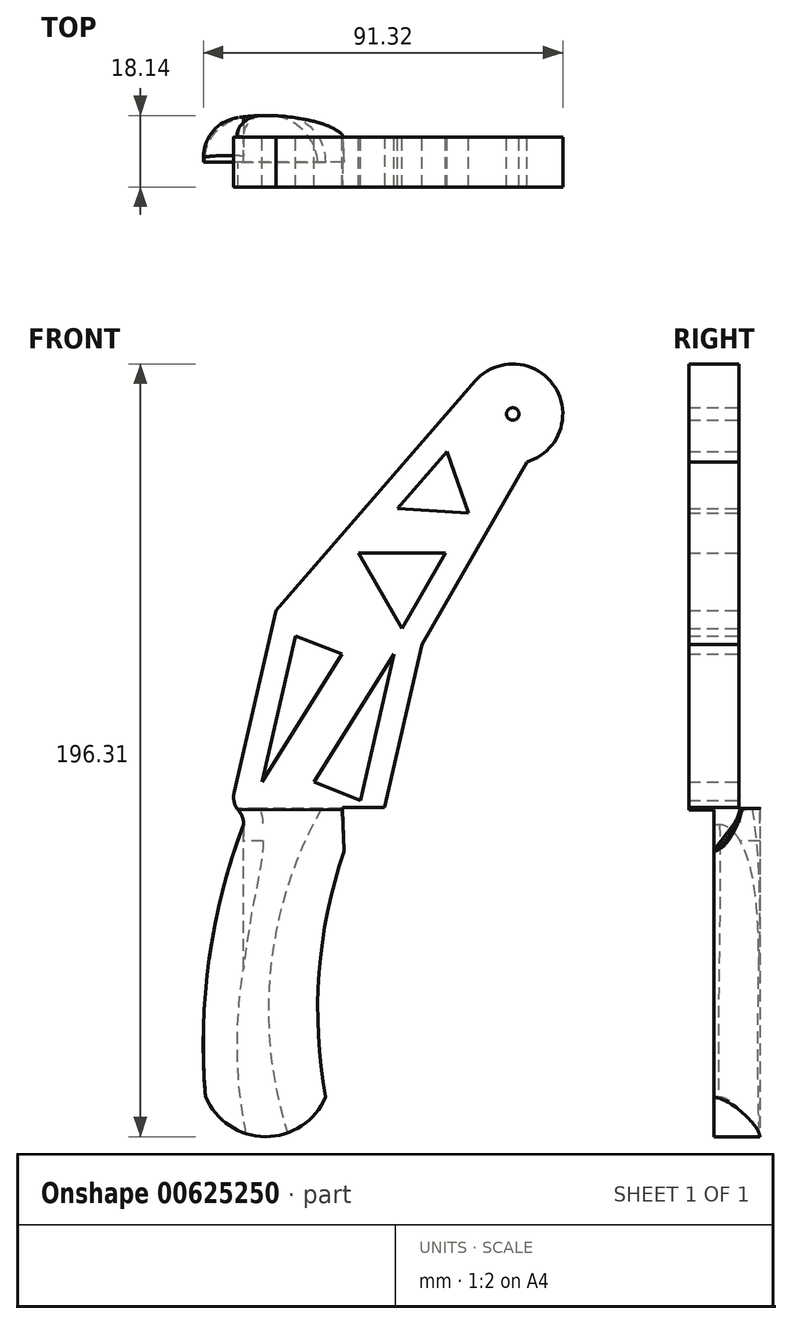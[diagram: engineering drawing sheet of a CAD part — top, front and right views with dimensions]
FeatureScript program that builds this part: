
annotation { "Feature Type Name" : "Feature", "Feature Type Description" : "" }
export const myFeature = defineFeature(function(context is Context, id is Id, definition is map)
    precondition{}
    {
        {
            var Q0;
            Q0=qCreatedBy(makeId("Front.planeOp"),FACE);
            var sketch = newSketch(context, id + "F0", { "sketchPlane" : qUnion([Q0])});
            skArc(sketch, "E0", {"start": v(128.28, -19.7) * mm, "mid": v(135.4, -0.67) * mm, "end": v(115.12, 0.81) * mm});
            skCircle(sketch, "E1", {"center": v(124.7, -7.52) * mm, "radius": 1.59 * mm});
            skLineSegment(sketch, "E2", {"start": v(115.12, 0.81) * mm, "end": v(64.49, -57.4) * mm});
            skLineSegment(sketch, "E3", {"start": v(64.49, -57.4) * mm, "end": v(53.2, -106.93) * mm});
            skLineSegment(sketch, "E4", {"start": v(128.28, -19.7) * mm, "end": v(101.6, -66.02) * mm});
            skPoint(sketch, "E4.endSnap0", {"position": v(101.6, 0) * mm});
            skLineSegment(sketch, "E5", {"start": v(101.6, -66.02) * mm, "end": v(92, -108.12) * mm});
            skArc(sketch, "E6", {"start": v(56.3, -111.86) * mm, "mid": v(47.6, -145.85) * mm, "end": v(46.64, -180.91) * mm});
            skLineSegment(sketch, "E7", {"start": v(53.2, -106.93) * mm, "end": v(56.3, -107.64) * mm});
            skLineSegment(sketch, "E8", {"start": v(56.3, -107.64) * mm, "end": v(56.3, -111.86) * mm});
            skLineSegment(sketch, "E9", {"start": v(92, -108.12) * mm, "end": v(85.97, -108.03) * mm});
            skArc(sketch, "E10", {"start": v(85.97, -108.03) * mm, "mid": v(76.06, -143.88) * mm, "end": v(77.12, -181.07) * mm});
            skArc(sketch, "E11", {"start": v(46.64, -180.91) * mm, "mid": v(61.83, -191.13) * mm, "end": v(77.12, -181.07) * mm});
            skLineSegment(sketch, "E12", {"start": v(107.95, -17.1) * mm, "end": v(95.44, -31.48) * mm});
            skLineSegment(sketch, "E13", {"start": v(107.95, -17.1) * mm, "end": v(113.5, -32.63) * mm});
            skLineSegment(sketch, "E14", {"start": v(95.44, -31.48) * mm, "end": v(113.5, -32.63) * mm});
            skLineSegment(sketch, "E15", {"start": v(107.61, -42.86) * mm, "end": v(96.59, -62) * mm});
            skPoint(sketch, "E15.startSnap0", {"position": v(114.94, -42.86) * mm});
            skLineSegment(sketch, "E16", {"start": v(96.59, -62) * mm, "end": v(85.53, -42.89) * mm});
            skLineSegment(sketch, "E17", {"start": v(85.53, -42.89) * mm, "end": v(107.61, -42.86) * mm});
            skLineSegment(sketch, "E18", {"start": v(69.52, -63.9) * mm, "end": v(61.05, -101.04) * mm});
            skLineSegment(sketch, "E19", {"start": v(61.05, -101.04) * mm, "end": v(81.35, -68.5) * mm});
            skLineSegment(sketch, "E20", {"start": v(81.35, -68.5) * mm, "end": v(69.52, -63.9) * mm});
            skLineSegment(sketch, "E21", {"start": v(94.52, -68.5) * mm, "end": v(74.22, -101.04) * mm});
            skLineSegment(sketch, "E22", {"start": v(74.22, -101.04) * mm, "end": v(86.05, -105.65) * mm});
            skLineSegment(sketch, "E23", {"start": v(86.05, -105.65) * mm, "end": v(94.52, -68.5) * mm});
            skSolve(sketch);
        }
        {
            var Q0;
            Q0 = qSketchRegion(id + "F0", true);
            extrude(context, id + "F1", {"entities" : qUnion([Q0]), "depth" : 19.05 * mm, "offsetDistance" : 25.4 * mm});
        }
        {
            var Q0;
            Q0=makeQuery(id+"F1.opExtrude","SWEPT_EDGE",EDGE,{"disambiguationData":[OSD([sQuery(id+"F0.wireOp",EDGE,"E7"),sQuery(id+"F0.wireOp",EDGE,"E8")])]});
            fillet(context, id + "F2", {"entities" : qUnion([Q0]), "radius" : 5.08 * mm, "tangentPropagation" : true, "allowEdgeOverflow" : false});
        }
        {
            var Q0;
            Q0=makeQuery(id+"F2.opFillet","BLEND_EDGE",EDGE,{"blendedFrom":[makeQuery(id+"F1.opExtrude","SWEPT_EDGE",EDGE,{"disambiguationData":[OSD([sQuery(id+"F0.wireOp",EDGE,"E7"),sQuery(id+"F0.wireOp",EDGE,"E8")])]}),makeQuery(id+"F1.opExtrude","SWEPT_FACE",FACE,{"disambiguationData":[OSD([sQuery(id+"F0.wireOp",EDGE,"E3")])]})],"blendedInto":[makeQuery(id+"F1.opExtrude","SWEPT_FACE",FACE,{"disambiguationData":[OSD([sQuery(id+"F0.wireOp",EDGE,"E3")])]})]});
            fillet(context, id + "F3", {"entities" : qUnion([Q0]), "radius" : 5.08 * mm, "tangentPropagation" : true, "allowEdgeOverflow" : false});
        }
        {
            var Q0;
            Q0=qCreatedBy(makeId("Top.planeOp"),FACE);
            cPlane(context, id + "F4", {"entities" : qUnion([Q0]), "cplaneType" : CPlaneType.OFFSET, "offset" : 192.53 * mm, "oppositeDirection" : true, "width" : 152.4 * mm, "height" : 152.4 * mm});
        }
        {
            var Q0;
            Q0=qCreatedBy(id+"F4.planeOp",FACE);
            var sketch = newSketch(context, id + "F5", { "sketchPlane" : qUnion([Q0])});
            skArc(sketch, "E24", {"start": v(81.46, -11.2) * mm, "mid": v(61.05, -7.27) * mm, "end": v(40.82, -12.06) * mm});
            skLineSegment(sketch, "E25", {"start": v(81.46, -11.2) * mm, "end": v(80.29, 11.88) * mm});
            skLineSegment(sketch, "E26", {"start": v(80.29, 11.88) * mm, "end": v(41.72, 10.68) * mm});
            skLineSegment(sketch, "E27", {"start": v(41.72, 10.68) * mm, "end": v(40.82, -12.06) * mm});
            skSolve(sketch);
        }
        {
            var Q0;
            Q0 = qSketchRegion(id + "F5", true);
            extrude(context, id + "F6", {"entities" : qUnion([Q0]), "operationType" : NewBodyOperationType.REMOVE, "depth" : 84.81 * mm, "offsetDistance" : 25.4 * mm});
        }
        {
            var Q0;
            Q0=makeQuery(id+"F1.opExtrude","CAP_FACE",FACE,{"disambiguationData":[OSD([sQuery(id+"F0.wireOp",EDGE,"E0"),sQuery(id+"F0.wireOp",EDGE,"E1"),sQuery(id+"F0.wireOp",EDGE,"E2"),sQuery(id+"F0.wireOp",EDGE,"E3"),sQuery(id+"F0.wireOp",EDGE,"E4"),sQuery(id+"F0.wireOp",EDGE,"E5"),sQuery(id+"F0.wireOp",EDGE,"E6"),sQuery(id+"F0.wireOp",EDGE,"E7"),sQuery(id+"F0.wireOp",EDGE,"E8"),sQuery(id+"F0.wireOp",EDGE,"E9"),sQuery(id+"F0.wireOp",EDGE,"E10"),sQuery(id+"F0.wireOp",EDGE,"E11"),sQuery(id+"F0.wireOp",EDGE,"E12"),sQuery(id+"F0.wireOp",EDGE,"E13"),sQuery(id+"F0.wireOp",EDGE,"E14"),sQuery(id+"F0.wireOp",EDGE,"E15"),sQuery(id+"F0.wireOp",EDGE,"E16"),sQuery(id+"F0.wireOp",EDGE,"E17"),sQuery(id+"F0.wireOp",EDGE,"E18"),sQuery(id+"F0.wireOp",EDGE,"E19"),sQuery(id+"F0.wireOp",EDGE,"E20"),sQuery(id+"F0.wireOp",EDGE,"E21"),sQuery(id+"F0.wireOp",EDGE,"E22"),sQuery(id+"F0.wireOp",EDGE,"E23")])],"isStart":true});
            var sketch = newSketch(context, id + "F7", { "sketchPlane" : qUnion([Q0])});
            skLineSegment(sketch, "E28", {"start": v(-80.9, -107.72) * mm, "end": v(-85.97, -108.03) * mm});
            skLineSegment(sketch, "E29", {"start": v(-85.97, -108.03) * mm, "end": v(-88.9, -122.3) * mm});
            skLineSegment(sketch, "E30", {"start": v(-88.9, -122.3) * mm, "end": v(-80.76, -122.3) * mm});
            skLineSegment(sketch, "E31", {"start": v(-80.76, -122.3) * mm, "end": v(-80.9, -107.72) * mm});
            skSolve(sketch);
        }
        {
            var Q0;
            Q0 = qSketchRegion(id + "F7", true);
            extrude(context, id + "F8", {"entities" : qUnion([Q0]), "operationType" : NewBodyOperationType.REMOVE, "oppositeDirection" : true, "depth" : 10.92 * mm, "offsetDistance" : 25.4 * mm});
        }
        {
            var Q0;
            Q0=makeQuery(id+"F6.boolean.opBoolean","COPY",FACE,{"derivedFrom":makeQuery(id+"F6.opExtrude","SWEPT_FACE",FACE,{"disambiguationData":[OSD([sQuery(id+"F5.wireOp",EDGE,"E25")])]})});
            var sketch = newSketch(context, id + "F9", { "sketchPlane" : qUnion([Q0])});
            skArc(sketch, "E32", {"start": v(16.7, -109.3) * mm, "mid": v(19.05, -114.53) * mm, "end": v(23.2, -118.49) * mm});
            skLineSegment(sketch, "E33", {"start": v(16.7, -109.3) * mm, "end": v(8.62, -109.3) * mm});
            skLineSegment(sketch, "E34", {"start": v(8.62, -109.3) * mm, "end": v(7.9, -127.1) * mm});
            skLineSegment(sketch, "E35", {"start": v(7.9, -127.1) * mm, "end": v(23.2, -118.49) * mm});
            skSolve(sketch);
        }
        {
            var Q0;
            Q0 = qSketchRegion(id + "F9", true);
            extrude(context, id + "F10", {"entities" : qUnion([Q0]), "operationType" : NewBodyOperationType.REMOVE, "oppositeDirection" : true, "depth" : 25.4 * mm, "offsetDistance" : 25.4 * mm});
        }
        {
            var Q0;
            Q0=makeQuery(id+"F10.boolean.opBoolean","INTERSECT",EDGE,{"derivedFrom":[makeQuery(id+"F1.opExtrude","SWEPT_FACE",FACE,{"disambiguationData":[OSD([sQuery(id+"F0.wireOp",EDGE,"E10")])]}),makeQuery(id+"F10.opExtrude","SWEPT_FACE",FACE,{"disambiguationData":[OSD([sQuery(id+"F9.wireOp",EDGE,"E32")])]})]});
            fillet(context, id + "F11", {"entities" : qUnion([Q0]), "radius" : 7.62 * mm, "tangentPropagation" : true, "allowEdgeOverflow" : false});
        }
        {
            var Q0;
            Q0=makeQuery(id+"F10.boolean.opBoolean","INTERSECT",EDGE,{"derivedFrom":[makeQuery(id+"F1.opExtrude","SWEPT_FACE",FACE,{"disambiguationData":[OSD([sQuery(id+"F0.wireOp",EDGE,"E10")])]}),makeQuery(id+"F10.opExtrude","SWEPT_FACE",FACE,{"disambiguationData":[OSD([sQuery(id+"F9.wireOp",EDGE,"E33")])]})]});
            fillet(context, id + "F12", {"entities" : qUnion([Q0]), "radius" : 5.08 * mm, "tangentPropagation" : true, "allowEdgeOverflow" : false});
        }
        {
            var Q0;
            {var subQ1=sQuery(id+"F7.wireOp",EDGE,"E28");var subQ2=makeQuery(id+"F1.opExtrude","SWEPT_FACE",FACE,{"disambiguationData":[OSD([sQuery(id+"F0.wireOp",EDGE,"E10")])]});Q0=makeQuery(id+"F12.opFillet","BLEND_EDGE",EDGE,{"blendedFrom":[makeQuery(id+"F10.boolean.opBoolean","INTERSECT",EDGE,{"derivedFrom":[subQ2,makeQuery(id+"F10.opExtrude","SWEPT_FACE",FACE,{"disambiguationData":[OSD([sQuery(id+"F9.wireOp",EDGE,"E33")])]})]}),makeQuery(id+"F8.boolean.opBoolean","COPY",FACE,{"disambiguationData":[TD([makeQuery(id+"F1.opExtrude","SWEPT_FACE",FACE,{"disambiguationData":[OSD([sQuery(id+"F0.wireOp",EDGE,"E9")])]})])],"derivedFrom":makeQuery(id+"F8.opExtrude","CAP_FACE",FACE,{"disambiguationData":[OSD([subQ1,sQuery(id+"F7.wireOp",EDGE,"E29"),sQuery(id+"F7.wireOp",EDGE,"E30"),sQuery(id+"F7.wireOp",EDGE,"E31")])],"isStart":false})})],"blendedInto":[makeQuery(id+"F8.boolean.opBoolean","COPY",FACE,{"disambiguationData":[TD([makeQuery(id+"F1.opExtrude","SWEPT_FACE",FACE,{"disambiguationData":[OSD([sQuery(id+"F0.wireOp",EDGE,"E9")])]})])],"derivedFrom":makeQuery(id+"F8.opExtrude","CAP_FACE",FACE,{"disambiguationData":[OSD([subQ1,sQuery(id+"F7.wireOp",EDGE,"E29"),sQuery(id+"F7.wireOp",EDGE,"E30"),sQuery(id+"F7.wireOp",EDGE,"E31")])],"isStart":false})})]});}
            var Q1;
            {var subQ1=sQuery(id+"F7.wireOp",EDGE,"E28");Q1=makeQuery(id+"F10.boolean.opBoolean","INTERSECT",EDGE,{"derivedFrom":[makeQuery(id+"F8.boolean.opBoolean","COPY",FACE,{"disambiguationData":[TD([makeQuery(id+"F1.opExtrude","SWEPT_FACE",FACE,{"disambiguationData":[OSD([sQuery(id+"F0.wireOp",EDGE,"E9")])]})])],"derivedFrom":makeQuery(id+"F8.opExtrude","CAP_FACE",FACE,{"disambiguationData":[OSD([subQ1,sQuery(id+"F7.wireOp",EDGE,"E29"),sQuery(id+"F7.wireOp",EDGE,"E30"),sQuery(id+"F7.wireOp",EDGE,"E31")])],"isStart":false})}),makeQuery(id+"F10.opExtrude","SWEPT_FACE",FACE,{"disambiguationData":[OSD([sQuery(id+"F9.wireOp",EDGE,"E33")])]})]});}
            fillet(context, id + "F13", {"entities" : qUnion([Q0, Q1]), "radius" : 1.27 * mm, "tangentPropagation" : true, "allowEdgeOverflow" : false});
        }
        {
            var Q0;
            Q0=makeQuery(id+"F1.opExtrude","CAP_FACE",FACE,{"disambiguationData":[OSD([sQuery(id+"F0.wireOp",EDGE,"E0"),sQuery(id+"F0.wireOp",EDGE,"E1"),sQuery(id+"F0.wireOp",EDGE,"E2"),sQuery(id+"F0.wireOp",EDGE,"E3"),sQuery(id+"F0.wireOp",EDGE,"E4"),sQuery(id+"F0.wireOp",EDGE,"E5"),sQuery(id+"F0.wireOp",EDGE,"E6"),sQuery(id+"F0.wireOp",EDGE,"E7"),sQuery(id+"F0.wireOp",EDGE,"E8"),sQuery(id+"F0.wireOp",EDGE,"E9"),sQuery(id+"F0.wireOp",EDGE,"E10"),sQuery(id+"F0.wireOp",EDGE,"E11"),sQuery(id+"F0.wireOp",EDGE,"E12"),sQuery(id+"F0.wireOp",EDGE,"E13"),sQuery(id+"F0.wireOp",EDGE,"E14"),sQuery(id+"F0.wireOp",EDGE,"E15"),sQuery(id+"F0.wireOp",EDGE,"E16"),sQuery(id+"F0.wireOp",EDGE,"E17"),sQuery(id+"F0.wireOp",EDGE,"E18"),sQuery(id+"F0.wireOp",EDGE,"E19"),sQuery(id+"F0.wireOp",EDGE,"E20"),sQuery(id+"F0.wireOp",EDGE,"E21"),sQuery(id+"F0.wireOp",EDGE,"E22"),sQuery(id+"F0.wireOp",EDGE,"E23")])],"isStart":true});
            var sketch = newSketch(context, id + "F14", { "sketchPlane" : qUnion([Q0])});
            skLineSegment(sketch, "E36", {"start": v(-54.63, -107.72) * mm, "end": v(-158.59, -107.87) * mm});
            skPoint(sketch, "E36.endSnap0", {"position": v(-83.43, -107.87) * mm});
            skLineSegment(sketch, "E37", {"start": v(-158.59, -107.87) * mm, "end": v(-152.02, 10.66) * mm});
            skLineSegment(sketch, "E38", {"start": v(-152.02, 10.66) * mm, "end": v(-99.2, 7.73) * mm});
            skLineSegment(sketch, "E39", {"start": v(-99.2, 7.73) * mm, "end": v(-29.43, -42.34) * mm});
            skLineSegment(sketch, "E40", {"start": v(-29.43, -42.34) * mm, "end": v(-46.2, -109.06) * mm});
            skLineSegment(sketch, "E41", {"start": v(-46.2, -109.06) * mm, "end": v(-54.63, -107.72) * mm});
            skSolve(sketch);
        }
        {
            var Q0;
            Q0 = qSketchRegion(id + "F14", true);
            extrude(context, id + "F15", {"entities" : qUnion([Q0]), "operationType" : NewBodyOperationType.REMOVE, "oppositeDirection" : true, "depth" : 12.7 * mm, "offsetDistance" : 25.4 * mm});
        }
        {
            var Q0;
            Q0=makeQuery(id+"F1.opExtrude","CAP_FACE",FACE,{"disambiguationData":[OSD([sQuery(id+"F0.wireOp",EDGE,"E0"),sQuery(id+"F0.wireOp",EDGE,"E1"),sQuery(id+"F0.wireOp",EDGE,"E2"),sQuery(id+"F0.wireOp",EDGE,"E3"),sQuery(id+"F0.wireOp",EDGE,"E4"),sQuery(id+"F0.wireOp",EDGE,"E5"),sQuery(id+"F0.wireOp",EDGE,"E6"),sQuery(id+"F0.wireOp",EDGE,"E7"),sQuery(id+"F0.wireOp",EDGE,"E8"),sQuery(id+"F0.wireOp",EDGE,"E9"),sQuery(id+"F0.wireOp",EDGE,"E10"),sQuery(id+"F0.wireOp",EDGE,"E11"),sQuery(id+"F0.wireOp",EDGE,"E12"),sQuery(id+"F0.wireOp",EDGE,"E13"),sQuery(id+"F0.wireOp",EDGE,"E14"),sQuery(id+"F0.wireOp",EDGE,"E15"),sQuery(id+"F0.wireOp",EDGE,"E16"),sQuery(id+"F0.wireOp",EDGE,"E17"),sQuery(id+"F0.wireOp",EDGE,"E18"),sQuery(id+"F0.wireOp",EDGE,"E19"),sQuery(id+"F0.wireOp",EDGE,"E20"),sQuery(id+"F0.wireOp",EDGE,"E21"),sQuery(id+"F0.wireOp",EDGE,"E22"),sQuery(id+"F0.wireOp",EDGE,"E23")])],"isStart":false});
            extrude(context, id + "F16", {"entities" : qUnion([Q0]), "operationType" : NewBodyOperationType.ADD, "depth" : 6.35 * mm, "offsetDistance" : 25.4 * mm});
        }
        {
            var Q0;
            Q0=makeQuery(id+"F16.opExtrude","CAP_FACE",FACE,{"disambiguationData":[OSD([sQuery(id+"F0.wireOp",EDGE,"E0"),sQuery(id+"F0.wireOp",EDGE,"E1"),sQuery(id+"F0.wireOp",EDGE,"E2"),sQuery(id+"F0.wireOp",EDGE,"E3"),sQuery(id+"F0.wireOp",EDGE,"E4"),sQuery(id+"F0.wireOp",EDGE,"E5"),sQuery(id+"F0.wireOp",EDGE,"E6"),sQuery(id+"F0.wireOp",EDGE,"E7"),sQuery(id+"F0.wireOp",EDGE,"E8"),sQuery(id+"F0.wireOp",EDGE,"E9"),sQuery(id+"F0.wireOp",EDGE,"E10"),sQuery(id+"F0.wireOp",EDGE,"E11"),sQuery(id+"F0.wireOp",EDGE,"E12"),sQuery(id+"F0.wireOp",EDGE,"E13"),sQuery(id+"F0.wireOp",EDGE,"E14"),sQuery(id+"F0.wireOp",EDGE,"E15"),sQuery(id+"F0.wireOp",EDGE,"E16"),sQuery(id+"F0.wireOp",EDGE,"E17"),sQuery(id+"F0.wireOp",EDGE,"E18"),sQuery(id+"F0.wireOp",EDGE,"E19"),sQuery(id+"F0.wireOp",EDGE,"E20"),sQuery(id+"F0.wireOp",EDGE,"E21"),sQuery(id+"F0.wireOp",EDGE,"E22"),sQuery(id+"F0.wireOp",EDGE,"E23")])],"isStart":false});
            var sketch = newSketch(context, id + "F17", { "sketchPlane" : qUnion([Q0])});
            skLineSegment(sketch, "E42", {"start": v(85.87, -108.11) * mm, "end": v(42.1, -108.03) * mm});
            skLineSegment(sketch, "E43", {"start": v(42.1, -108.03) * mm, "end": v(20.57, -203.22) * mm});
            skLineSegment(sketch, "E44", {"start": v(20.57, -203.22) * mm, "end": v(103.95, -212.14) * mm});
            skLineSegment(sketch, "E45", {"start": v(85.87, -108.11) * mm, "end": v(103.95, -212.14) * mm});
            skSolve(sketch);
        }
        {
            var Q0;
            Q0 = qSketchRegion(id + "F17", true);
            extrude(context, id + "F18", {"entities" : qUnion([Q0]), "operationType" : NewBodyOperationType.REMOVE, "oppositeDirection" : true, "depth" : 6.35 * mm, "offsetDistance" : 25.4 * mm});
        }
        {
            var Q0;
            Q0=qCreatedBy(makeId("Front.planeOp"),FACE);
            var sketch = newSketch(context, id + "F19", { "sketchPlane" : qUnion([Q0])});
            skLineSegment(sketch, "E46", {"start": v(81.87, -118.5) * mm, "end": v(81.43, -107.44) * mm});
            skLineSegment(sketch, "E47", {"start": v(81.43, -107.44) * mm, "end": v(92.86, -107.44) * mm});
            skLineSegment(sketch, "E48", {"start": v(92.86, -107.44) * mm, "end": v(81.87, -118.5) * mm});
            skSolve(sketch);
        }
        {
            var Q0;
            Q0 = qSketchRegion(id + "F19", true);
            extrude(context, id + "F20", {"entities" : qUnion([Q0]), "operationType" : NewBodyOperationType.REMOVE, "depth" : 87.38 * mm, "offsetDistance" : 25.4 * mm});
        }
        {
            var Q0;
            {var subQ0=makeQuery(id+"F1.opExtrude","SWEPT_FACE",FACE,{"disambiguationData":[OSD([sQuery(id+"F0.wireOp",EDGE,"E10")])]});var subQ1=makeQuery(id+"F6.opExtrude","SWEPT_FACE",FACE,{"disambiguationData":[OSD([sQuery(id+"F5.wireOp",EDGE,"E24")])]});Q0=makeQuery(id+"F8.boolean.opBoolean","SPLIT",EDGE,{"disambiguationData":[TD([makeQuery(id+"F1.opExtrude","SWEPT_FACE",FACE,{"disambiguationData":[OSD([sQuery(id+"F0.wireOp",EDGE,"E11")])]})])],"derivedFrom":makeQuery(id+"F6.boolean.opBoolean","INTERSECT",EDGE,{"derivedFrom":[subQ0,subQ1]})});}
            fillet(context, id + "F21", {"entities" : qUnion([Q0]), "radius" : 12.7 * mm, "tangentPropagation" : true, "allowEdgeOverflow" : false});
        }
        {
            var Q0;
            {var subQ0=makeQuery(id+"F1.opExtrude","SWEPT_FACE",FACE,{"disambiguationData":[OSD([sQuery(id+"F0.wireOp",EDGE,"E10")])]});var subQ1=makeQuery(id+"F6.opExtrude","SWEPT_FACE",FACE,{"disambiguationData":[OSD([sQuery(id+"F5.wireOp",EDGE,"E24")])]});Q0=makeQuery(id+"F21.opFillet","BLEND_EDGE",EDGE,{"blendedFrom":[makeQuery(id+"F8.boolean.opBoolean","SPLIT",EDGE,{"disambiguationData":[TD([makeQuery(id+"F1.opExtrude","SWEPT_FACE",FACE,{"disambiguationData":[OSD([sQuery(id+"F0.wireOp",EDGE,"E11")])]})])],"derivedFrom":makeQuery(id+"F6.boolean.opBoolean","INTERSECT",EDGE,{"derivedFrom":[subQ0,subQ1]})}),makeQuery(id+"F10.boolean.opBoolean","COPY",FACE,{"derivedFrom":makeQuery(id+"F10.opExtrude","CAP_FACE",FACE,{"disambiguationData":[OSD([sQuery(id+"F9.wireOp",EDGE,"E32"),sQuery(id+"F9.wireOp",EDGE,"E33"),sQuery(id+"F9.wireOp",EDGE,"E34"),sQuery(id+"F9.wireOp",EDGE,"E35")])],"isStart":true})})],"blendedInto":[makeQuery(id+"F10.boolean.opBoolean","COPY",FACE,{"derivedFrom":makeQuery(id+"F10.opExtrude","CAP_FACE",FACE,{"disambiguationData":[OSD([sQuery(id+"F9.wireOp",EDGE,"E32"),sQuery(id+"F9.wireOp",EDGE,"E33"),sQuery(id+"F9.wireOp",EDGE,"E34"),sQuery(id+"F9.wireOp",EDGE,"E35")])],"isStart":true})})]});}
            fillet(context, id + "F22", {"entities" : qUnion([Q0]), "radius" : 1.27 * mm, "tangentPropagation" : true, "allowEdgeOverflow" : false});
        }
        {
            var Q0;
            Q0=makeQuery(id+"F6.boolean.opBoolean","INTERSECT",EDGE,{"derivedFrom":[makeQuery(id+"F1.opExtrude","SWEPT_FACE",FACE,{"disambiguationData":[OSD([sQuery(id+"F0.wireOp",EDGE,"E6")])]}),makeQuery(id+"F6.opExtrude","SWEPT_FACE",FACE,{"disambiguationData":[OSD([sQuery(id+"F5.wireOp",EDGE,"E24")])]})]});
            fillet(context, id + "F23", {"entities" : qUnion([Q0]), "radius" : 10.16 * mm, "tangentPropagation" : true, "allowEdgeOverflow" : false});
        }
        {
            var Q0;
            Q0=makeQuery(id+"F6.boolean.opBoolean","INTERSECT",EDGE,{"derivedFrom":[makeQuery(id+"F1.opExtrude","SWEPT_FACE",FACE,{"disambiguationData":[OSD([sQuery(id+"F0.wireOp",EDGE,"E8")])]}),makeQuery(id+"F6.opExtrude","SWEPT_FACE",FACE,{"disambiguationData":[OSD([sQuery(id+"F5.wireOp",EDGE,"E24")])]})]});
            fillet(context, id + "F24", {"entities" : qUnion([Q0]), "radius" : 5.08 * mm, "tangentPropagation" : true, "allowEdgeOverflow" : false});
        }
    });
